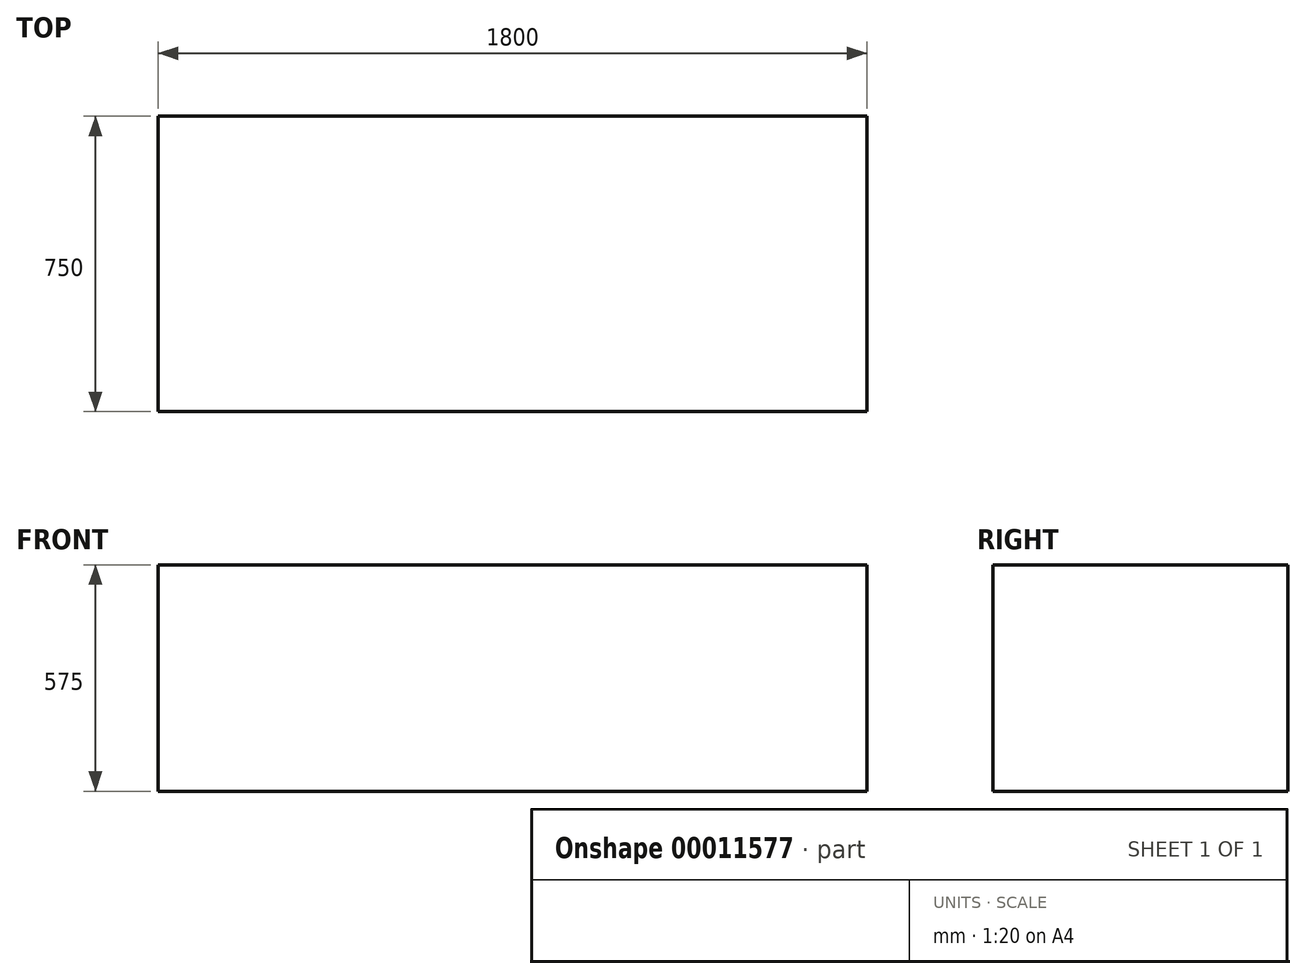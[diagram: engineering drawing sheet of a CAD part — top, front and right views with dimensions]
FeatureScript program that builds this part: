
annotation { "Feature Type Name" : "Feature", "Feature Type Description" : "" }
export const myFeature = defineFeature(function(context is Context, id is Id, definition is map)
    precondition{}
    {
        {
            var Q0;
            Q0=qCreatedBy(makeId("Right.planeOp"),FACE);
            var sketch = newSketch(context, id + "F0", { "sketchPlane" : qUnion([Q0])});
            skLineSegment(sketch, "E0.rect.bottom", {"start": v(-375, 287.5) * mm, "end": v(375, 287.5) * mm});
            skLineSegment(sketch, "E0.rect.top", {"start": v(-375, -287.5) * mm, "end": v(375, -287.5) * mm});
            skLineSegment(sketch, "E0.rect.left", {"start": v(-375, 287.5) * mm, "end": v(-375, -287.5) * mm});
            skLineSegment(sketch, "E0.rect.right", {"start": v(375, 287.5) * mm, "end": v(375, -287.5) * mm});
            skPoint(sketch, "E0.rect.middle", {"position": v(0, 0) * mm});
            skSolve(sketch);
        }
        {
            var Q0;
            Q0=makeQuery(id+"F0.imprint","IMPRINT",FACE,{"disambiguationData":[TD([[makeQuery(id+"F0.imprint","IMPRINT",EDGE,{"derivedFrom":sQuery(id+"F0.wireOp",EDGE,"E0.rect.bottom")}),-1.0]])]});
            extrude(context, id + "F1", {"entities" : qUnion([Q0]), "depth" : 1800 * mm});
        }
    });
